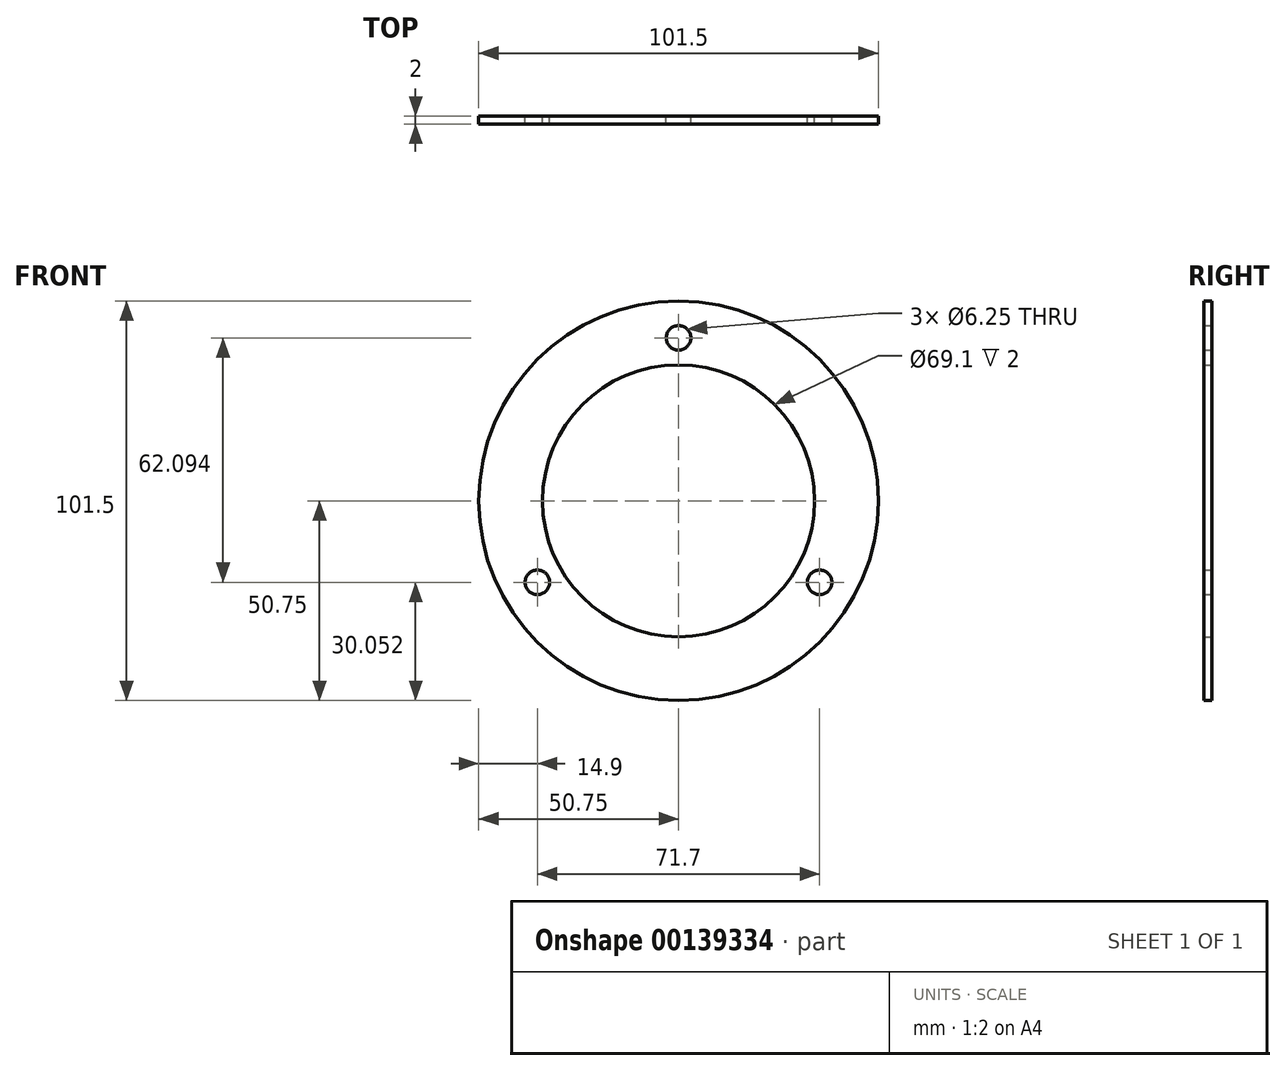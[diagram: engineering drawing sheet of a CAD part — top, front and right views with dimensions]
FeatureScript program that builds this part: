
annotation { "Feature Type Name" : "Feature", "Feature Type Description" : "" }
export const myFeature = defineFeature(function(context is Context, id is Id, definition is map)
    precondition{}
    {
        {
            var Q0;
            Q0=qCreatedBy(makeId("Front.planeOp"),FACE);
            var sketch = newSketch(context, id + "F0", { "sketchPlane" : qUnion([Q0])});
            skCircle(sketch, "E0", {"center": v(0, 0) * mm, "radius": 50.75 * mm});
            skCircle(sketch, "E1", {"center": v(0, 41.4) * mm, "radius": 3.12 * mm});
            skCircle(sketch, "E2", {"center": v(35.85, -20.7) * mm, "radius": 3.12 * mm});
            skCircle(sketch, "E3", {"center": v(-35.85, -20.7) * mm, "radius": 3.12 * mm});
            skLineSegment(sketch, "E4", {"start": v(0, 41.4) * mm, "end": v(0, 0) * mm});
            skLineSegment(sketch, "E5", {"start": v(-35.85, -20.7) * mm, "end": v(0, 0) * mm});
            skLineSegment(sketch, "E6", {"start": v(35.85, -20.7) * mm, "end": v(0, 0) * mm});
            skCircle(sketch, "E7.0", {"center": v(0, 0) * mm, "radius": 34.55 * mm});
            skLineSegment(sketch, "E8", {"start": v(0, 34.55) * mm, "end": v(0, 34.55) * mm});
            skPoint(sketch, "E9", {"position": v(0, 34.55) * mm});
            skLineSegment(sketch, "E10", {"start": v(29.92, -17.27) * mm, "end": v(29.92, -17.27) * mm});
            skLineSegment(sketch, "E11", {"start": v(-29.92, -17.27) * mm, "end": v(-29.92, -17.28) * mm});
            skPoint(sketch, "E12", {"position": v(29.92, -17.27) * mm});
            skPoint(sketch, "E13", {"position": v(-29.92, -17.27) * mm});
            skSolve(sketch);
        }
        {
            var Q0;
            Q0=makeQuery(id+"F0.imprint","IMPRINT",FACE,{"disambiguationData":[TD([[makeQuery(id+"F0.imprint","IMPRINT",EDGE,{"derivedFrom":sQuery(id+"F0.wireOp",EDGE,"E0")}),1.0]])]});
            var Q1;
            {var subQ0=sQuery(id+"F0.wireOp",EDGE,"E4");var subQ1=sQuery(id+"F0.wireOp",EDGE,"E1");var subQ2=makeQuery(id+"F0.imprint","INTERSECT",VERTEX,{"derivedFrom":[subQ1,subQ0]});Q1=makeQuery(id+"F0.imprint","IMPRINT",FACE,{"disambiguationData":[TD([[makeQuery(id+"F0.imprint","IMPRINT",EDGE,{"disambiguationData":[TD([[subQ2,1.0]])],"derivedFrom":subQ1}),-1.0]])]});}
            var Q2;
            {var subQ0=sQuery(id+"F0.wireOp",EDGE,"E4");var subQ1=sQuery(id+"F0.wireOp",EDGE,"E1");var subQ2=makeQuery(id+"F0.imprint","INTERSECT",VERTEX,{"derivedFrom":[subQ1,subQ0]});Q2=makeQuery(id+"F0.imprint","IMPRINT",FACE,{"disambiguationData":[TD([[makeQuery(id+"F0.imprint","IMPRINT",EDGE,{"disambiguationData":[TD([[subQ2,-1.0]])],"derivedFrom":subQ1}),-1.0]])]});}
            var Q3;
            {var subQ0=sQuery(id+"F0.wireOp",EDGE,"E5");var subQ1=sQuery(id+"F0.wireOp",EDGE,"E3");var subQ2=makeQuery(id+"F0.imprint","INTERSECT",VERTEX,{"derivedFrom":[subQ1,subQ0]});Q3=makeQuery(id+"F0.imprint","IMPRINT",FACE,{"disambiguationData":[TD([[makeQuery(id+"F0.imprint","IMPRINT",EDGE,{"disambiguationData":[TD([[subQ2,-1.0]])],"derivedFrom":subQ1}),-1.0]])]});}
            var Q4;
            {var subQ0=sQuery(id+"F0.wireOp",EDGE,"E5");var subQ1=sQuery(id+"F0.wireOp",EDGE,"E3");var subQ2=makeQuery(id+"F0.imprint","INTERSECT",VERTEX,{"derivedFrom":[subQ1,subQ0]});Q4=makeQuery(id+"F0.imprint","IMPRINT",FACE,{"disambiguationData":[TD([[makeQuery(id+"F0.imprint","IMPRINT",EDGE,{"disambiguationData":[TD([[subQ2,1.0]])],"derivedFrom":subQ1}),-1.0]])]});}
            var Q5;
            {var subQ0=sQuery(id+"F0.wireOp",EDGE,"E6");var subQ1=sQuery(id+"F0.wireOp",EDGE,"E2");var subQ2=makeQuery(id+"F0.imprint","INTERSECT",VERTEX,{"derivedFrom":[subQ1,subQ0]});Q5=makeQuery(id+"F0.imprint","IMPRINT",FACE,{"disambiguationData":[TD([[makeQuery(id+"F0.imprint","IMPRINT",EDGE,{"disambiguationData":[TD([[subQ2,-1.0]])],"derivedFrom":subQ1}),-1.0]])]});}
            var Q6;
            {var subQ0=sQuery(id+"F0.wireOp",EDGE,"E6");var subQ1=sQuery(id+"F0.wireOp",EDGE,"E2");var subQ2=makeQuery(id+"F0.imprint","INTERSECT",VERTEX,{"derivedFrom":[subQ1,subQ0]});Q6=makeQuery(id+"F0.imprint","IMPRINT",FACE,{"disambiguationData":[TD([[makeQuery(id+"F0.imprint","IMPRINT",EDGE,{"disambiguationData":[TD([[subQ2,1.0]])],"derivedFrom":subQ1}),-1.0]])]});}
            extrude(context, id + "F1", {"entities" : qUnion([Q0, Q1, Q2, Q3, Q4, Q5, Q6]), "depth" : 2 * mm});
        }
    });
